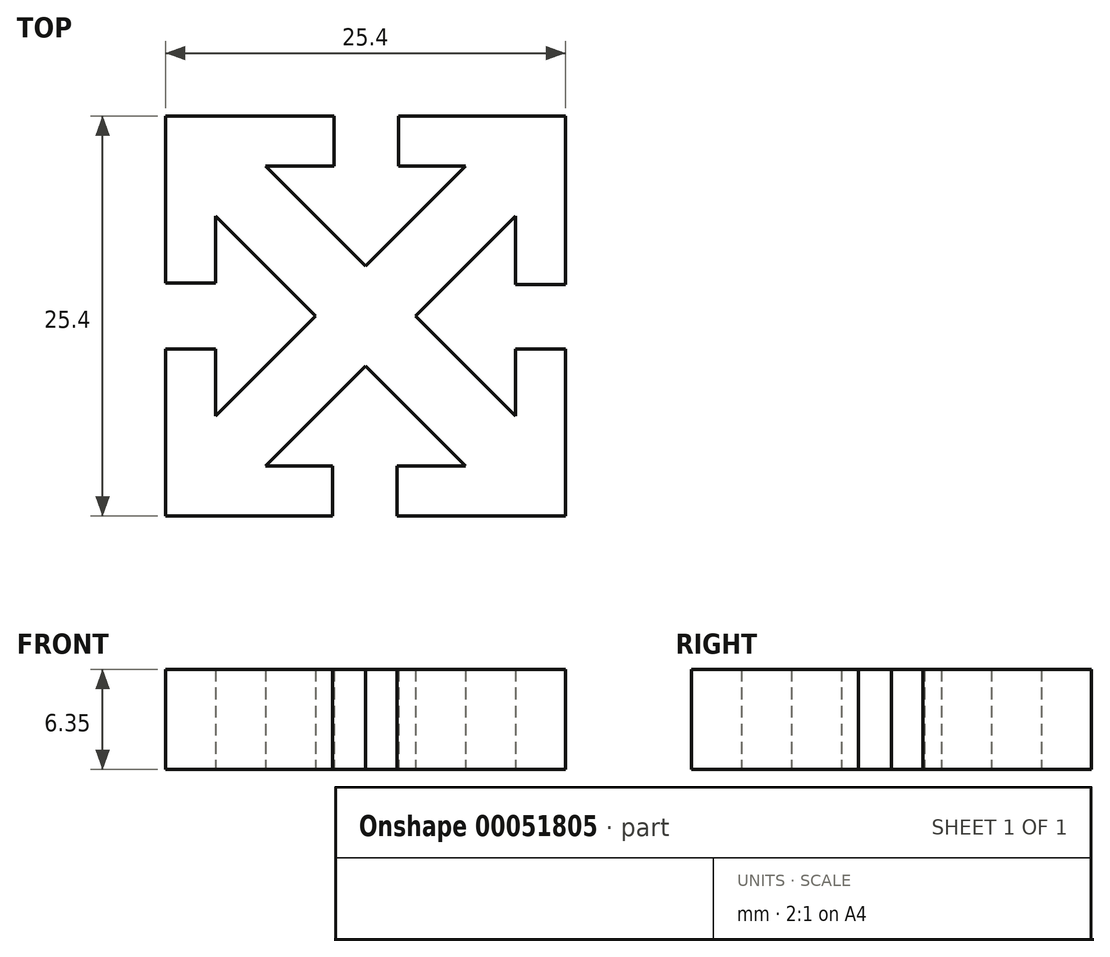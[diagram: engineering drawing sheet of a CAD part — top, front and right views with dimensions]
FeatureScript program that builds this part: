
annotation { "Feature Type Name" : "Feature", "Feature Type Description" : "" }
export const myFeature = defineFeature(function(context is Context, id is Id, definition is map)
    precondition{}
    {
        {
            var Q0;
            Q0=qCreatedBy(makeId("Top.planeOp"),FACE);
            var sketch = newSketch(context, id + "F0", { "sketchPlane" : qUnion([Q0])});
            skLineSegment(sketch, "E0.rect.bottom", {"start": v(12.7, 12.7) * mm, "end": v(-12.7, 12.7) * mm});
            skLineSegment(sketch, "E0.rect.top", {"start": v(12.7, -12.7) * mm, "end": v(-12.7, -12.7) * mm});
            skLineSegment(sketch, "E0.rect.left", {"start": v(12.7, 12.7) * mm, "end": v(12.7, -12.7) * mm});
            skLineSegment(sketch, "E0.rect.right", {"start": v(-12.7, 12.7) * mm, "end": v(-12.7, -12.7) * mm});
            skPoint(sketch, "E0.rect.middle", {"position": v(0, 0) * mm});
            skLineSegment(sketch, "E1.rect.bottom", {"start": v(9.52, 9.53) * mm, "end": v(-9.53, 9.53) * mm});
            skLineSegment(sketch, "E1.rect.top", {"start": v(9.52, -9.53) * mm, "end": v(-9.53, -9.53) * mm});
            skLineSegment(sketch, "E1.rect.left", {"start": v(9.53, 9.53) * mm, "end": v(9.53, -9.53) * mm});
            skLineSegment(sketch, "E1.rect.right", {"start": v(-9.53, 9.53) * mm, "end": v(-9.53, -9.53) * mm});
            skLineSegment(sketch, "E2.bottom", {"start": v(-12.7, 12.7) * mm, "end": v(-9.53, 12.7) * mm});
            skLineSegment(sketch, "E2.top", {"start": v(-12.7, 9.53) * mm, "end": v(-9.53, 9.53) * mm});
            skLineSegment(sketch, "E2.left", {"start": v(-12.7, 12.7) * mm, "end": v(-12.7, 9.53) * mm});
            skLineSegment(sketch, "E2.right", {"start": v(-9.53, 12.7) * mm, "end": v(-9.53, 9.53) * mm});
            skLineSegment(sketch, "E3.bottom", {"start": v(12.7, 12.7) * mm, "end": v(9.52, 12.7) * mm});
            skLineSegment(sketch, "E3.top", {"start": v(12.7, 9.53) * mm, "end": v(9.52, 9.53) * mm});
            skLineSegment(sketch, "E3.left", {"start": v(12.7, 12.7) * mm, "end": v(12.7, 9.53) * mm});
            skLineSegment(sketch, "E3.right", {"start": v(9.52, 12.7) * mm, "end": v(9.52, 9.53) * mm});
            skLineSegment(sketch, "E4.bottom", {"start": v(12.7, -12.7) * mm, "end": v(9.52, -12.7) * mm});
            skLineSegment(sketch, "E4.top", {"start": v(12.7, -9.53) * mm, "end": v(9.52, -9.53) * mm});
            skLineSegment(sketch, "E4.left", {"start": v(12.7, -12.7) * mm, "end": v(12.7, -9.53) * mm});
            skLineSegment(sketch, "E4.right", {"start": v(9.52, -12.7) * mm, "end": v(9.52, -9.53) * mm});
            skLineSegment(sketch, "E5.bottom", {"start": v(-12.7, -12.7) * mm, "end": v(-9.53, -12.7) * mm});
            skLineSegment(sketch, "E5.top", {"start": v(-12.7, -9.53) * mm, "end": v(-9.53, -9.53) * mm});
            skLineSegment(sketch, "E5.left", {"start": v(-12.7, -12.7) * mm, "end": v(-12.7, -9.53) * mm});
            skLineSegment(sketch, "E5.right", {"start": v(-9.53, -12.7) * mm, "end": v(-9.53, -9.53) * mm});
            skLineSegment(sketch, "E6", {"start": v(-9.52, 12.7) * mm, "end": v(12.7, -9.52) * mm});
            skLineSegment(sketch, "E7", {"start": v(9.52, -12.7) * mm, "end": v(-12.7, 9.52) * mm});
            skLineSegment(sketch, "E8", {"start": v(-12.7, -9.52) * mm, "end": v(9.52, 12.7) * mm});
            skLineSegment(sketch, "E9", {"start": v(12.7, 9.52) * mm, "end": v(-9.52, -12.7) * mm});
            skSolve(sketch);
        }
        {
            var Q0;
            Q0=makeQuery(id+"F0.imprint","IMPRINT",FACE,{"disambiguationData":[TD([[makeQuery(id+"F0.imprint","IMPRINT",EDGE,{"derivedFrom":sQuery(id+"F0.wireOp",EDGE,"E2.bottom")}),-1.0]])]});
            var Q1;
            Q1=makeQuery(id+"F0.imprint","IMPRINT",FACE,{"disambiguationData":[TD([[makeQuery(id+"F0.imprint","IMPRINT",EDGE,{"derivedFrom":sQuery(id+"F0.wireOp",EDGE,"E3.bottom")}),1.0]])]});
            var Q2;
            Q2=makeQuery(id+"F0.imprint","IMPRINT",FACE,{"disambiguationData":[TD([[makeQuery(id+"F0.imprint","IMPRINT",EDGE,{"derivedFrom":sQuery(id+"F0.wireOp",EDGE,"E4.bottom")}),-1.0]])]});
            var Q3;
            Q3=makeQuery(id+"F0.imprint","IMPRINT",FACE,{"disambiguationData":[TD([[makeQuery(id+"F0.imprint","IMPRINT",EDGE,{"derivedFrom":sQuery(id+"F0.wireOp",EDGE,"E5.bottom")}),1.0]])]});
            var Q4;
            {var subQ0=sQuery(id+"F0.wireOp",EDGE,"E0.rect.bottom");Q4=makeQuery(id+"F0.imprint","IMPRINT",FACE,{"disambiguationData":[TD([[makeQuery(id+"F0.imprint","IMPRINT",EDGE,{"derivedFrom":subQ0}),1.0]])]});}
            var Q5;
            {var subQ0=sQuery(id+"F0.wireOp",EDGE,"E0.rect.top");Q5=makeQuery(id+"F0.imprint","IMPRINT",FACE,{"disambiguationData":[TD([[makeQuery(id+"F0.imprint","IMPRINT",EDGE,{"derivedFrom":subQ0}),-1.0]])]});}
            var Q6;
            {var subQ0=sQuery(id+"F0.wireOp",EDGE,"E0.rect.left");Q6=makeQuery(id+"F0.imprint","IMPRINT",FACE,{"disambiguationData":[TD([[makeQuery(id+"F0.imprint","IMPRINT",EDGE,{"derivedFrom":subQ0}),-1.0]])]});}
            var Q7;
            {var subQ0=sQuery(id+"F0.wireOp",EDGE,"E0.rect.right");Q7=makeQuery(id+"F0.imprint","IMPRINT",FACE,{"disambiguationData":[TD([[makeQuery(id+"F0.imprint","IMPRINT",EDGE,{"derivedFrom":subQ0}),1.0]])]});}
            var Q8;
            {var subQ0=sQuery(id+"F0.wireOp",EDGE,"E3.right");Q8=makeQuery(id+"F0.imprint","IMPRINT",FACE,{"disambiguationData":[TD([[makeQuery(id+"F0.imprint","IMPRINT",EDGE,{"derivedFrom":subQ0}),-1.0]])]});}
            var Q9;
            {var subQ0=sQuery(id+"F0.wireOp",EDGE,"E2.right");Q9=makeQuery(id+"F0.imprint","IMPRINT",FACE,{"disambiguationData":[TD([[makeQuery(id+"F0.imprint","IMPRINT",EDGE,{"derivedFrom":subQ0}),1.0]])]});}
            var Q10;
            {var subQ0=sQuery(id+"F0.wireOp",EDGE,"E4.right");Q10=makeQuery(id+"F0.imprint","IMPRINT",FACE,{"disambiguationData":[TD([[makeQuery(id+"F0.imprint","IMPRINT",EDGE,{"derivedFrom":subQ0}),1.0]])]});}
            var Q11;
            {var subQ0=sQuery(id+"F0.wireOp",EDGE,"E5.right");Q11=makeQuery(id+"F0.imprint","IMPRINT",FACE,{"disambiguationData":[TD([[makeQuery(id+"F0.imprint","IMPRINT",EDGE,{"derivedFrom":subQ0}),-1.0]])]});}
            var Q12;
            {var subQ0=sQuery(id+"F0.wireOp",EDGE,"E3.top");Q12=makeQuery(id+"F0.imprint","IMPRINT",FACE,{"disambiguationData":[TD([[makeQuery(id+"F0.imprint","IMPRINT",EDGE,{"derivedFrom":subQ0}),1.0]])]});}
            var Q13;
            {var subQ0=sQuery(id+"F0.wireOp",EDGE,"E4.top");Q13=makeQuery(id+"F0.imprint","IMPRINT",FACE,{"disambiguationData":[TD([[makeQuery(id+"F0.imprint","IMPRINT",EDGE,{"derivedFrom":subQ0}),-1.0]])]});}
            var Q14;
            {var subQ0=sQuery(id+"F0.wireOp",EDGE,"E2.top");Q14=makeQuery(id+"F0.imprint","IMPRINT",FACE,{"disambiguationData":[TD([[makeQuery(id+"F0.imprint","IMPRINT",EDGE,{"derivedFrom":subQ0}),-1.0]])]});}
            var Q15;
            {var subQ0=sQuery(id+"F0.wireOp",EDGE,"E5.top");Q15=makeQuery(id+"F0.imprint","IMPRINT",FACE,{"disambiguationData":[TD([[makeQuery(id+"F0.imprint","IMPRINT",EDGE,{"derivedFrom":subQ0}),1.0]])]});}
            var Q16;
            {var subQ0=sQuery(id+"F0.wireOp",EDGE,"E8");var subQ3=sQuery(id+"F0.wireOp",EDGE,"E6");var subQ4=makeQuery(id+"F0.imprint","INTERSECT",VERTEX,{"derivedFrom":[subQ3,subQ0]});Q16=makeQuery(id+"F0.imprint","IMPRINT",FACE,{"disambiguationData":[TD([[makeQuery(id+"F0.imprint","IMPRINT",EDGE,{"disambiguationData":[TD([[subQ4,-1.0]])],"derivedFrom":subQ3}),1.0]])]});}
            var Q17;
            {var subQ5=sQuery(id+"F0.wireOp",EDGE,"E6");var subQ6=sQuery(id+"F0.wireOp",EDGE,"E1.rect.bottom");var subQ7=makeQuery(id+"F0.imprint","INTERSECT",VERTEX,{"derivedFrom":[subQ6,subQ5]});Q17=makeQuery(id+"F0.imprint","IMPRINT",FACE,{"disambiguationData":[TD([[makeQuery(id+"F0.imprint","IMPRINT",EDGE,{"disambiguationData":[TD([[subQ7,-1.0]])],"derivedFrom":subQ5}),-1.0]])]});}
            var Q18;
            {var subQ5=sQuery(id+"F0.wireOp",EDGE,"E1.rect.left");var subQ7=sQuery(id+"F0.wireOp",EDGE,"E6");var subQ8=makeQuery(id+"F0.imprint","INTERSECT",VERTEX,{"derivedFrom":[subQ5,subQ7]});Q18=makeQuery(id+"F0.imprint","IMPRINT",FACE,{"disambiguationData":[TD([[makeQuery(id+"F0.imprint","IMPRINT",EDGE,{"disambiguationData":[TD([[subQ8,1.0]])],"derivedFrom":subQ7}),-1.0]])]});}
            var Q19;
            {var subQ0=sQuery(id+"F0.wireOp",EDGE,"E8");var subQ1=sQuery(id+"F0.wireOp",EDGE,"E6");var subQ2=makeQuery(id+"F0.imprint","INTERSECT",VERTEX,{"derivedFrom":[subQ1,subQ0]});Q19=makeQuery(id+"F0.imprint","IMPRINT",FACE,{"disambiguationData":[TD([[makeQuery(id+"F0.imprint","IMPRINT",EDGE,{"disambiguationData":[TD([[subQ2,-1.0]])],"derivedFrom":subQ1}),-1.0]])]});}
            var Q20;
            {var subQ0=sQuery(id+"F0.wireOp",EDGE,"E9");var subQ1=sQuery(id+"F0.wireOp",EDGE,"E7");var subQ2=makeQuery(id+"F0.imprint","INTERSECT",VERTEX,{"derivedFrom":[subQ1,subQ0]});Q20=makeQuery(id+"F0.imprint","IMPRINT",FACE,{"disambiguationData":[TD([[makeQuery(id+"F0.imprint","IMPRINT",EDGE,{"disambiguationData":[TD([[subQ2,-1.0]])],"derivedFrom":subQ1}),1.0]])]});}
            extrude(context, id + "F1", {"entities" : qUnion([Q0, Q1, Q2, Q3, Q4, Q5, Q6, Q7, Q8, Q9, Q10, Q11, Q12, Q13, Q14, Q15, Q16, Q17, Q18, Q19, Q20]), "depth" : 6.35 * mm});
        }
        {
            var Q0;
            Q0=makeQuery(id+"F1.opExtrude","CAP_FACE",FACE,{"disambiguationData":[OSD([sQuery(id+"F0.wireOp",EDGE,"E0.rect.bottom"),sQuery(id+"F0.wireOp",EDGE,"E0.rect.top"),sQuery(id+"F0.wireOp",EDGE,"E0.rect.left"),sQuery(id+"F0.wireOp",EDGE,"E0.rect.right"),sQuery(id+"F0.wireOp",EDGE,"E1.rect.bottom"),sQuery(id+"F0.wireOp",EDGE,"E1.rect.top"),sQuery(id+"F0.wireOp",EDGE,"E1.rect.left"),sQuery(id+"F0.wireOp",EDGE,"E1.rect.right"),sQuery(id+"F0.wireOp",EDGE,"E2.bottom"),sQuery(id+"F0.wireOp",EDGE,"E2.left"),sQuery(id+"F0.wireOp",EDGE,"E3.bottom"),sQuery(id+"F0.wireOp",EDGE,"E3.left"),sQuery(id+"F0.wireOp",EDGE,"E4.bottom"),sQuery(id+"F0.wireOp",EDGE,"E4.left"),sQuery(id+"F0.wireOp",EDGE,"E5.bottom"),sQuery(id+"F0.wireOp",EDGE,"E5.left"),sQuery(id+"F0.wireOp",EDGE,"E6"),sQuery(id+"F0.wireOp",EDGE,"E7"),sQuery(id+"F0.wireOp",EDGE,"E8"),sQuery(id+"F0.wireOp",EDGE,"E9")])],"isStart":true});
            var sketch = newSketch(context, id + "F2", { "sketchPlane" : qUnion([Q0])});
            skLineSegment(sketch, "E10.left", {"start": v(9.52, 6.35) * mm, "end": v(9.52, -6.23) * mm});
            skLineSegment(sketch, "E10.right", {"start": v(12.7, 6.35) * mm, "end": v(12.7, -6.23) * mm});
            skLineSegment(sketch, "E11.rect.bottom", {"start": v(12.7, -1.99) * mm, "end": v(9.53, -1.99) * mm});
            skLineSegment(sketch, "E11.rect.top", {"start": v(12.7, 2.1) * mm, "end": v(9.53, 2.1) * mm});
            skLineSegment(sketch, "E11.rect.left", {"start": v(12.7, -1.99) * mm, "end": v(12.7, 2.1) * mm});
            skLineSegment(sketch, "E11.rect.right", {"start": v(9.53, -1.99) * mm, "end": v(9.53, 2.1) * mm});
            skPoint(sketch, "E11.rect.middle", {"position": v(11.11, 0.06) * mm});
            skLineSegment(sketch, "E12.MirrorCS", {"start": v(-12.7, 2.1) * mm, "end": v(-9.53, 2.1) * mm});
            skLineSegment(sketch, "E13.MirrorCS", {"start": v(-9.53, -1.99) * mm, "end": v(-9.53, 2.1) * mm});
            skLineSegment(sketch, "E14.MirrorCS", {"start": v(-12.7, -1.99) * mm, "end": v(-9.53, -1.99) * mm});
            skLineSegment(sketch, "E15.MirrorCS", {"start": v(-12.7, -1.99) * mm, "end": v(-12.7, 2.1) * mm});
            skLineSegment(sketch, "E16.1.0", {"start": v(-2.1, 12.7) * mm, "end": v(-2.1, 9.53) * mm});
            skLineSegment(sketch, "E16.1.1", {"start": v(1.99, 9.53) * mm, "end": v(-2.1, 9.53) * mm});
            skLineSegment(sketch, "E16.1.2", {"start": v(1.99, 12.7) * mm, "end": v(1.99, 9.53) * mm});
            skLineSegment(sketch, "E16.1.3", {"start": v(1.99, 12.7) * mm, "end": v(-2.1, 12.7) * mm});
            skLineSegment(sketch, "E16.2.0", {"start": v(-12.7, -2.1) * mm, "end": v(-9.53, -2.1) * mm});
            skLineSegment(sketch, "E16.2.1", {"start": v(-9.53, 1.99) * mm, "end": v(-9.53, -2.1) * mm});
            skLineSegment(sketch, "E16.2.2", {"start": v(-12.7, 1.99) * mm, "end": v(-9.53, 1.99) * mm});
            skLineSegment(sketch, "E16.2.3", {"start": v(-12.7, 1.99) * mm, "end": v(-12.7, -2.1) * mm});
            skLineSegment(sketch, "E16.3.0", {"start": v(2.1, -12.7) * mm, "end": v(2.1, -9.53) * mm});
            skLineSegment(sketch, "E16.3.1", {"start": v(-1.99, -9.53) * mm, "end": v(2.1, -9.53) * mm});
            skLineSegment(sketch, "E16.3.2", {"start": v(-1.99, -12.7) * mm, "end": v(-1.99, -9.53) * mm});
            skLineSegment(sketch, "E16.3.3", {"start": v(-1.99, -12.7) * mm, "end": v(2.1, -12.7) * mm});
            skPoint(sketch, "E16.center", {"position": v(0, 0) * mm});
            skSolve(sketch);
        }
        {
            var Q0;
            Q0 = qSketchRegion(id + "F2", true);
            extrude(context, id + "F3", {"entities" : qUnion([Q0]), "operationType" : NewBodyOperationType.REMOVE, "oppositeDirection" : true, "depth" : 25.4 * mm});
        }
    });
